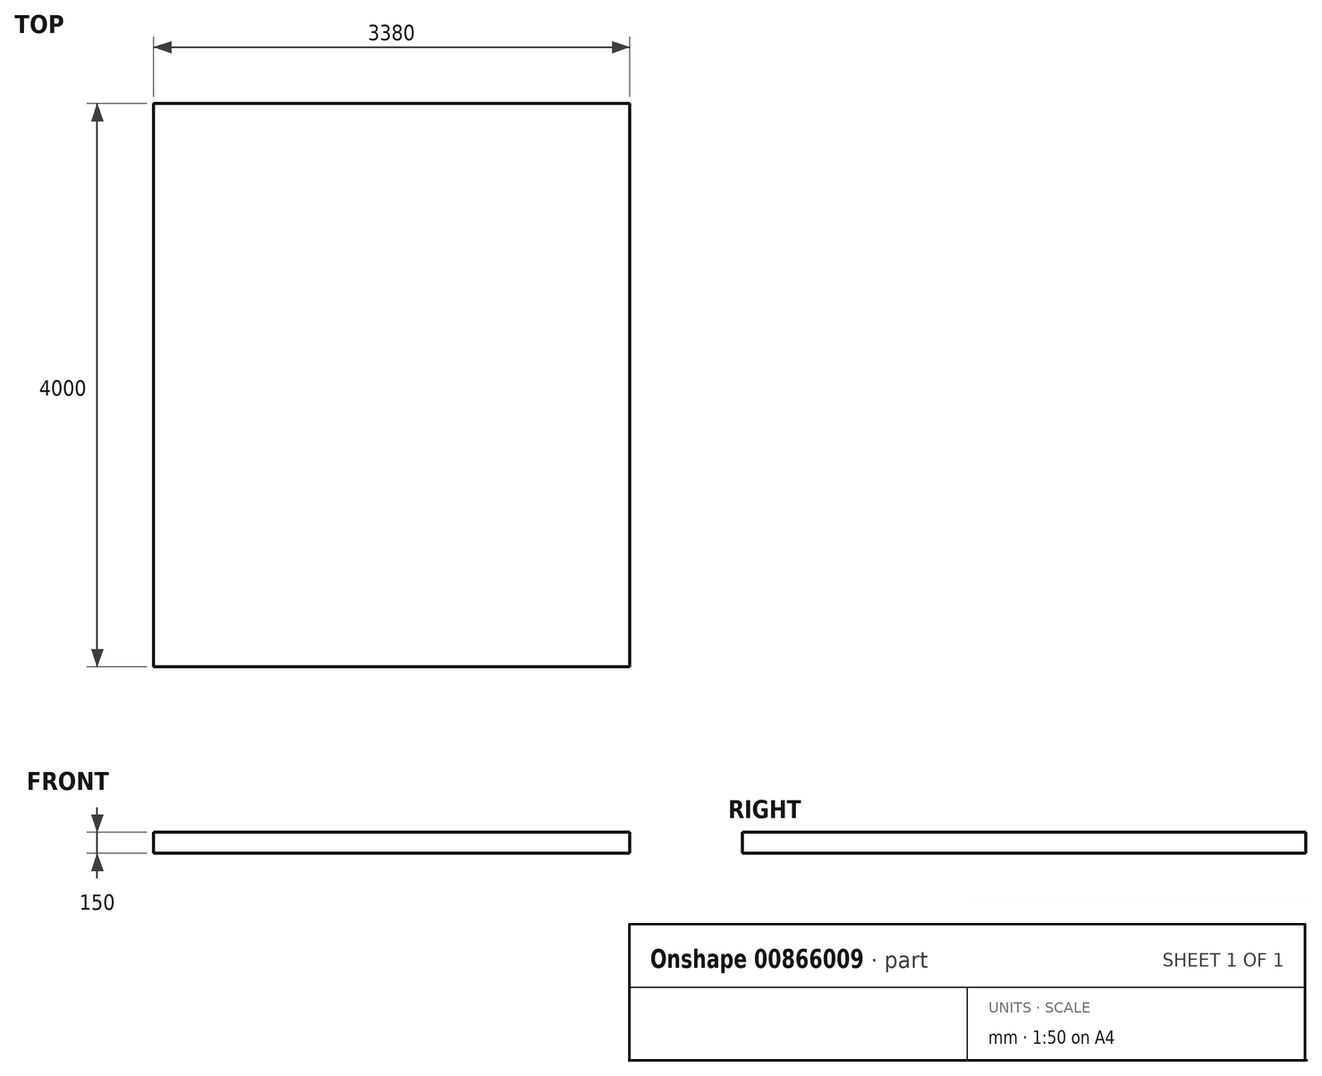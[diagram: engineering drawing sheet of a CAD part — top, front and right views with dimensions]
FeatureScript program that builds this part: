
annotation { "Feature Type Name" : "Feature", "Feature Type Description" : "" }
export const myFeature = defineFeature(function(context is Context, id is Id, definition is map)
    precondition{}
    {
        {
            var Q0;
            Q0=qCreatedBy(makeId("Front.planeOp"),FACE);
            var sketch = newSketch(context, id + "F0", { "sketchPlane" : qUnion([Q0])});
            skLineSegment(sketch, "E0.bottom", {"start": v(0, 0) * mm, "end": v(-3380, 0) * mm});
            skLineSegment(sketch, "E0.top", {"start": v(0, -150) * mm, "end": v(-3380, -150) * mm});
            skLineSegment(sketch, "E0.left", {"start": v(0, 0) * mm, "end": v(0, -150) * mm});
            skLineSegment(sketch, "E0.right", {"start": v(-3380, 0) * mm, "end": v(-3380, -150) * mm});
            skSolve(sketch);
        }
        {
            var Q0;
            Q0 = qSketchRegion(id + "F0", true);
            extrude(context, id + "F1", {"entities" : qUnion([Q0]), "depth" : 4000 * mm, "offsetDistance" : 25 * mm});
        }
    });
